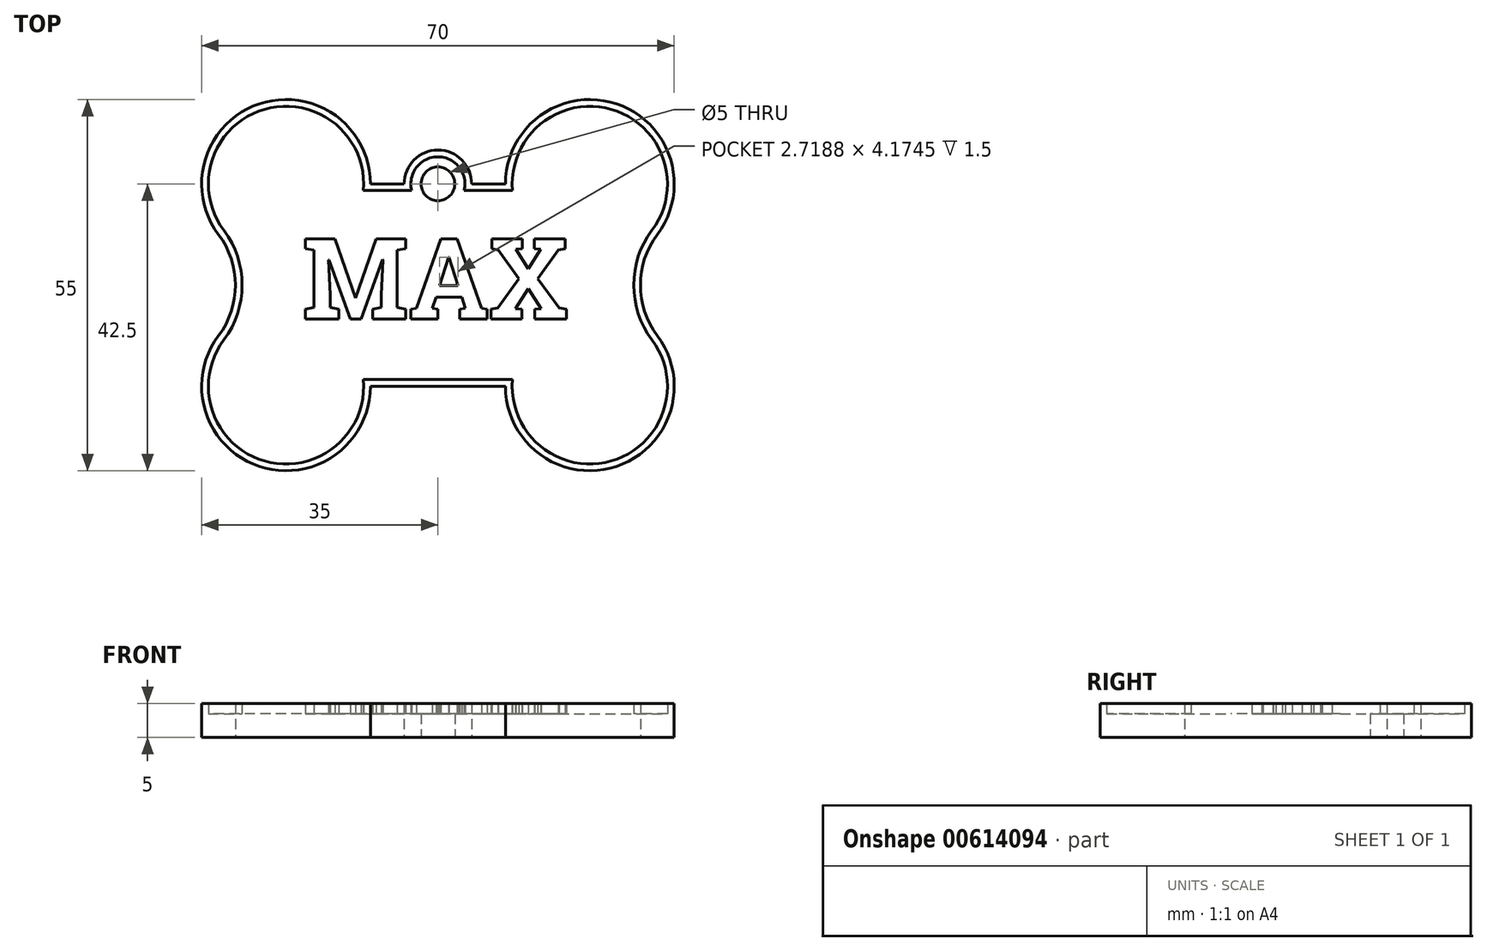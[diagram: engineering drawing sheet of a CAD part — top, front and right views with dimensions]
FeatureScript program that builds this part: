
annotation { "Feature Type Name" : "Feature", "Feature Type Description" : "" }
export const myFeature = defineFeature(function(context is Context, id is Id, definition is map)
    precondition{}
    {
        {
            var Q0;
            Q0=qCreatedBy(makeId("Top.planeOp"),FACE);
            var sketch = newSketch(context, id + "F0", { "sketchPlane" : qUnion([Q0])});
            skArc(sketch, "E0", {"start": v(22.5, 30) * mm, "mid": v(6.05, 41.86) * mm, "end": v(0, 22.5) * mm});
            skArc(sketch, "E1", {"start": v(65, 22.5) * mm, "mid": v(58.95, 41.86) * mm, "end": v(42.5, 30) * mm});
            skArc(sketch, "E2", {"start": v(0, 7.5) * mm, "mid": v(6.05, -11.86) * mm, "end": v(22.5, 0) * mm});
            skArc(sketch, "E3", {"start": v(42.5, 0) * mm, "mid": v(58.95, -11.86) * mm, "end": v(65, 7.5) * mm});
            skArc(sketch, "E4", {"start": v(0, 7.5) * mm, "mid": v(2.5, 15) * mm, "end": v(0, 22.5) * mm});
            skPoint(sketch, "E4.first.point", {"position": v(0, 22.5) * mm});
            skPoint(sketch, "E4.second.point", {"position": v(0, 7.5) * mm});
            skPoint(sketch, "E4.third.point", {"position": v(-18.54, 24.13) * mm});
            skArc(sketch, "E5", {"start": v(65, 22.5) * mm, "mid": v(62.5, 15) * mm, "end": v(65, 7.5) * mm});
            skPoint(sketch, "E5.first.point", {"position": v(65, 22.5) * mm});
            skPoint(sketch, "E5.second.point", {"position": v(65, 7.5) * mm});
            skPoint(sketch, "E5.third.point", {"position": v(87.38, 16.75) * mm});
            skLineSegment(sketch, "E6.trimOffspring", {"start": v(22.5, 0) * mm, "end": v(42.5, 0) * mm});
            skLineSegment(sketch, "E7.trimOffspring", {"start": v(42.5, 30) * mm, "end": v(37.5, 30) * mm});
            skCircle(sketch, "E8", {"center": v(32.5, 30) * mm, "radius": 2.5 * mm});
            skArc(sketch, "E9", {"start": v(37.5, 30) * mm, "mid": v(32.5, 35) * mm, "end": v(27.5, 30) * mm});
            skLineSegment(sketch, "E10.trimOffspring", {"start": v(27.5, 30) * mm, "end": v(22.5, 30) * mm});
            skSolve(sketch);
        }
        {
            var Q0;
            Q0 = qSketchRegion(id + "F0", true);
            extrude(context, id + "F1", {"entities" : qUnion([Q0]), "depth" : 3.5 * mm, "offsetDistance" : 25 * mm});
        }
        {
            var Q0;
            Q0=makeQuery(id+"F1.opExtrude","CAP_FACE",FACE,{"disambiguationData":[OSD([sQuery(id+"F0.wireOp",EDGE,"E0"),sQuery(id+"F0.wireOp",EDGE,"E1"),sQuery(id+"F0.wireOp",EDGE,"E2"),sQuery(id+"F0.wireOp",EDGE,"E3"),sQuery(id+"F0.wireOp",EDGE,"E4"),sQuery(id+"F0.wireOp",EDGE,"E5"),sQuery(id+"F0.wireOp",EDGE,"E6.trimOffspring"),sQuery(id+"F0.wireOp",EDGE,"E7.trimOffspring"),sQuery(id+"F0.wireOp",EDGE,"E8"),sQuery(id+"F0.wireOp",EDGE,"E9"),sQuery(id+"F0.wireOp",EDGE,"E10.trimOffspring")])],"isStart":false});
            var sketch = newSketch(context, id + "F2", { "sketchPlane" : qUnion([Q0])});
            skText(sketch, "E11", { "text": "MAX", "fontName": "RobotoSlab-Bold.ttf"});
            skArc(sketch, "E12.0", {"start": v(43.54, 1) * mm, "mid": v(58.16, -11.06) * mm, "end": v(64.2, 6.9) * mm});
            skLineSegment(sketch, "E12.1", {"start": v(21.46, 1) * mm, "end": v(43.54, 1) * mm});
            skArc(sketch, "E12.2", {"start": v(64.2, 6.9) * mm, "mid": v(61.5, 15) * mm, "end": v(64.2, 23.1) * mm});
            skArc(sketch, "E12.3", {"start": v(0.8, 6.9) * mm, "mid": v(6.84, -11.06) * mm, "end": v(21.46, 1) * mm});
            skArc(sketch, "E12.4", {"start": v(0.8, 23.1) * mm, "mid": v(3.5, 15) * mm, "end": v(0.8, 6.9) * mm});
            skArc(sketch, "E12.5", {"start": v(21.46, 29) * mm, "mid": v(6.84, 41.06) * mm, "end": v(0.8, 23.1) * mm});
            skArc(sketch, "E12.6", {"start": v(64.2, 23.1) * mm, "mid": v(58.16, 41.06) * mm, "end": v(43.54, 29) * mm});
            skLineSegment(sketch, "E12.7", {"start": v(43.54, 29) * mm, "end": v(36.37, 29) * mm});
            skArc(sketch, "E12.8", {"start": v(36.37, 29) * mm, "mid": v(32.5, 34) * mm, "end": v(28.63, 29) * mm});
            skLineSegment(sketch, "E12.9", {"start": v(28.63, 29) * mm, "end": v(21.46, 29) * mm});
            const initialGuessF2  = {"E11": [0.01244, 0.01, 1, 0, 0.012]};
            skSetInitialGuess(sketch, initialGuessF2);
            skSolve(sketch);
        }
        {
            var Q0;
            Q0=makeQuery(id+"F2.imprint","IMPRINT",FACE,{"disambiguationData":[TD([[makeQuery(id+"F2.imprint","IMPRINT",EDGE,{"derivedFrom":sQuery(id+"F2.wireOp",EDGE,"E12.0")}),-1.0]])]});
            var Q1;
            Q1=makeQuery(id+"F2.imprint","IMPRINT",FACE,{"disambiguationData":[TD([[makeQuery(id+"F2.imprint","IMPRINT",EDGE,{"derivedFrom":sQuery(id+"F2.wireOp",EDGE,"E11.sketch_text.stroke-0")}),-1.0]])]});
            var Q2;
            Q2=makeQuery(id+"F2.imprint","IMPRINT",FACE,{"disambiguationData":[TD([[makeQuery(id+"F2.imprint","IMPRINT",EDGE,{"derivedFrom":sQuery(id+"F2.wireOp",EDGE,"E11.sketch_text.stroke-31")}),-1.0]])]});
            var Q3;
            Q3=makeQuery(id+"F2.imprint","IMPRINT",FACE,{"disambiguationData":[TD([[makeQuery(id+"F2.imprint","IMPRINT",EDGE,{"derivedFrom":sQuery(id+"F2.wireOp",EDGE,"E11.sketch_text.stroke-51")}),-1.0]])]});
            extrude(context, id + "F3", {"entities" : qUnion([Q0, Q1, Q2, Q3]), "operationType" : NewBodyOperationType.ADD, "depth" : 1.5 * mm, "offsetDistance" : 25 * mm});
        }
    });
